# Revit family: MADEL_GRILL_AIR RETURN_FIXED BLADES 45º_DMT+(PLRX - PLRXL) – (3.D1)_0
name_source: partatom
category: Air Terminals
revit_build: Autodesk Revit 2015 (Build: 20140606_1530(x64)
units: mm (PartAtom-declared; Revit-internal decimal feet)

## types (10) — shared parameters
BIMETRICAL = http://www.bimetrical.com
BIMETRICAL Category = AirTerminal
Description = MADEL_Fixed blades air return grilles
Family Version = 1.0
IfcExportAs = IfcAirTerminalType
IfcExportType = IfcAirTerminalType
Manufacturer = MADEL
Material Grill = MADEL_M9016
Material Plenum Box = <By Category>
Nº Plenum Connections = 3
Review Date = 11/2016
Revit Version = Revit 2015 - English
Type Comments = The DMT series grilles are designed to be used in extractors of cold and hot air. They are mounted on walls or in false ceilings.
Type Image = <None>
URL = http://www.madel.com
Vmax = 3.0 m/s
Vmed = 2.3 m/s
Vmin = 1.5 m/s
b_factor = -0.128138
m_factor = 1.899495

## per-type parameters (varying)
| type | Afree | B | Blade Lenght | D1 | D_Connector | E | H | H1 | H2 | Kf | L | L3 | Max Flow | Min Flow | N_Graphic lines | Nº  Blades | PLRX | PLRX/L | Plenum Connection Type | Product Size |
| DMT-AR+PLRX 1200x150 | 0.1023 m² | 1230 mm  [stored 4.03543 ft] | 1185 mm | 123 mm  [stored 0.403543 ft] | 125 mm  [stored 0.410105 ft] | 170 mm  [stored 0.557743 ft] | 150 mm | 135 mm  [stored 0.442913 ft] | 27 mm  [stored 0.0885827 ft] | 0.752929 | 1200 mm | 1185 mm | 1,105 m³/h | 553 m³/h | 4 | 5 | Yes | No | Upper | 1200x150 |
| DMT-AR+PLRX 1200x100 | 0.0644 m² | 1230 mm  [stored 4.03543 ft] | 1185 mm | 98 mm  [stored 0.321522 ft] | 100 mm  [stored 0.328084 ft] | 120 mm | 100 mm  [stored 0.328084 ft] | 85 mm  [stored 0.278871 ft] | 21.3 mm | -1.249544 | 1200 mm | 1185 mm | 695 m³/h | 348 m³/h | 3 | 3 | Yes | No | Upper | 1200x100 |
| DMT-AR+PLRX 1100x150 | 0.0937 m² | 1130 mm  [stored 3.70735 ft] | 1085 mm  [stored 3.55971 ft] | 123 mm  [stored 0.403543 ft] | 125 mm  [stored 0.410105 ft] | 170 mm  [stored 0.557743 ft] | 150 mm | 135 mm  [stored 0.442913 ft] | 27 mm  [stored 0.0885827 ft] | 0.372587 | 1100 mm | 1085 mm  [stored 3.55971 ft] | 1,012 m³/h | 506 m³/h | 4 | 5 | Yes | No | Upper | 1100x150 |
| DMT-AR+PLRX 1100x100 | 0.0590 m² | 1130 mm  [stored 3.70735 ft] | 1085 mm  [stored 3.55971 ft] | 98 mm  [stored 0.321522 ft] | 100 mm  [stored 0.328084 ft] | 120 mm | 100 mm  [stored 0.328084 ft] | 85 mm  [stored 0.278871 ft] | 21.3 mm | -1.629207 | 1100 mm | 1085 mm  [stored 3.55971 ft] | 637 m³/h | 318 m³/h | 3 | 3 | Yes | No | Upper | 1100x100 |
| DMT-AR+PLRX/L 1200x300 | 0.2161 m² | 1230 mm  [stored 4.03543 ft] | 1185 mm | 248 mm | 250 mm  [stored 0.82021 ft] | 320 mm  [stored 1.04987 ft] | 300 mm | 285 mm  [stored 0.935039 ft] | 31.7 mm | 3.985618 | 1200 mm | 1185 mm | 2,334 m³/h | 1,167 m³/h | 8 | 11 | No | Yes | Lateral | 1200x300 |
| DMT-AR+PLRX/L 1200x250 | 0.1782 m² | 1230 mm  [stored 4.03543 ft] | 1185 mm | 248 mm | 250 mm  [stored 0.82021 ft] | 270 mm  [stored 0.885827 ft] | 250 mm  [stored 0.82021 ft] | 235 mm  [stored 0.770997 ft] | 33.6 mm | 3.15119 | 1200 mm | 1185 mm | 1,924 m³/h | 962 m³/h | 6 | 9 | No | Yes | Lateral | 1200x250 |
| DMT-AR+PLRX/L 1200x200 | 0.1403 m² | 1230 mm  [stored 4.03543 ft] | 1185 mm | 198 mm | 200 mm  [stored 0.656168 ft] | 220 mm  [stored 0.721785 ft] | 200 mm  [stored 0.656168 ft] | 185 mm  [stored 0.606955 ft] | 30.8 mm | 2.116257 | 1200 mm | 1185 mm | 1,515 m³/h | 757 m³/h | 5 | 7 | No | Yes | Lateral | 1200x200 |
| DMT-AR+PLRX/L 1200x150 | 0.1023 m² | 1230 mm  [stored 4.03543 ft] | 1185 mm | 198 mm | 200 mm  [stored 0.656168 ft] | 170 mm  [stored 0.557743 ft] | 150 mm | 135 mm  [stored 0.442913 ft] | 27 mm  [stored 0.0885827 ft] | 0.752929 | 1200 mm | 1185 mm | 1,105 m³/h | 553 m³/h | 4 | 5 | No | Yes | Lateral | 1200x150 |
| DMT-AR+PLRX/L 1200x100 | 0.0644 m² | 1230 mm  [stored 4.03543 ft] | 1185 mm | 198 mm | 200 mm  [stored 0.656168 ft] | 120 mm | 100 mm  [stored 0.328084 ft] | 85 mm  [stored 0.278871 ft] | 21.3 mm | -1.249544 | 1200 mm | 1185 mm | 695 m³/h | 348 m³/h | 3 | 3 | No | Yes | Lateral | 1200x100 |
| DMT-AR+PLRX/L 1100x150 | 0.0937 m² | 1130 mm  [stored 3.70735 ft] | 1085 mm  [stored 3.55971 ft] | 198 mm | 200 mm  [stored 0.656168 ft] | 170 mm  [stored 0.557743 ft] | 150 mm | 135 mm  [stored 0.442913 ft] | 27 mm  [stored 0.0885827 ft] | 0.372587 | 1100 mm | 1085 mm  [stored 3.55971 ft] | 1,012 m³/h | 506 m³/h | 4 | 5 | No | Yes | Lateral | 1100x150 |

note: column(s) folded — value = type name in every type: Model

note: [stored X ft] marks values corroborated as IEEE doubles in the binary element streams (Revit-internal decimal feet)

## geometry (parser evidence)
native form markers: Blend x2
no freeform markers — native parametric forms only
